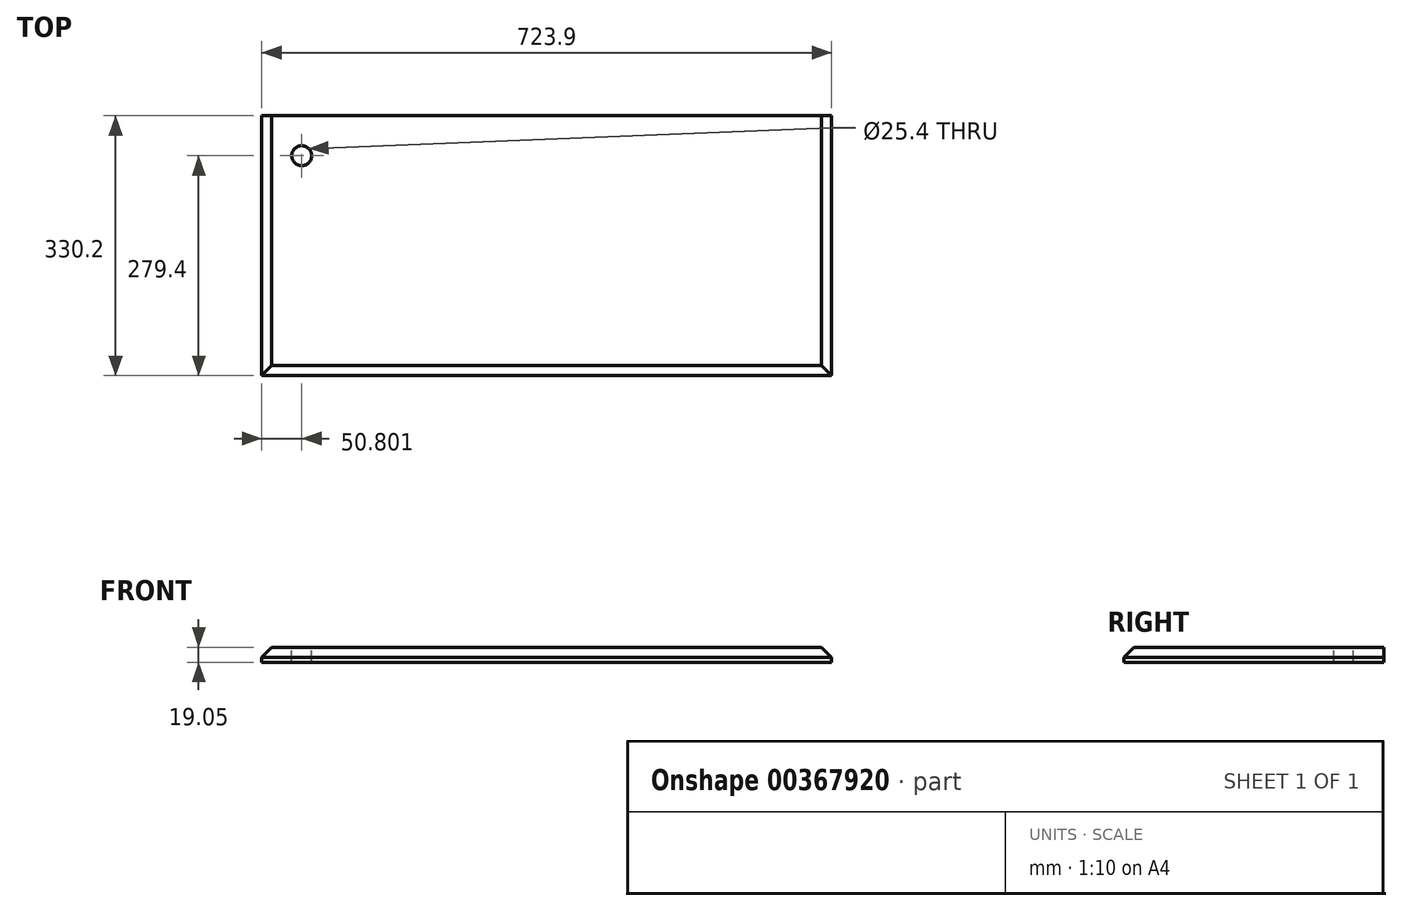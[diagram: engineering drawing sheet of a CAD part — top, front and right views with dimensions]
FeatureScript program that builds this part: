
annotation { "Feature Type Name" : "Feature", "Feature Type Description" : "" }
export const myFeature = defineFeature(function(context is Context, id is Id, definition is map)
    precondition{}
    {
        {
            var Q0;
            Q0=qCreatedBy(makeId("Top.planeOp"),FACE);
            var sketch = newSketch(context, id + "F0", { "sketchPlane" : qUnion([Q0])});
            skLineSegment(sketch, "E0.bottom", {"start": v(-327.98, 161.44) * mm, "end": v(395.92, 161.44) * mm});
            skLineSegment(sketch, "E0.top", {"start": v(-327.98, -168.76) * mm, "end": v(395.92, -168.76) * mm});
            skLineSegment(sketch, "E0.left", {"start": v(-327.98, 161.44) * mm, "end": v(-327.98, -168.76) * mm});
            skLineSegment(sketch, "E0.right", {"start": v(395.92, 161.44) * mm, "end": v(395.92, -168.76) * mm});
            skPoint(sketch, "E1", {"position": v(-277.18, 110.64) * mm});
            skSolve(sketch);
        }
        {
            var Q0;
            Q0 = qSketchRegion(id + "F0", true);
            extrude(context, id + "F1", {"entities" : qUnion([Q0]), "depth" : 19.05 * mm});
        }
        {
            var Q0;
            Q0=makeQuery(id+"F1.opExtrude","CAP_EDGE",EDGE,{"disambiguationData":[OSD([sQuery(id+"F0.wireOp",EDGE,"E0.right")])],"isStart":false});
            var Q1;
            Q1=makeQuery(id+"F1.opExtrude","CAP_EDGE",EDGE,{"disambiguationData":[OSD([sQuery(id+"F0.wireOp",EDGE,"E0.left")])],"isStart":false});
            var Q2;
            Q2=makeQuery(id+"F1.opExtrude","CAP_EDGE",EDGE,{"disambiguationData":[OSD([sQuery(id+"F0.wireOp",EDGE,"E0.top")])],"isStart":false});
            chamfer(context, id + "F2", {"entities" : qUnion([Q0, Q1, Q2]), "width" : 12.7 * mm, "tangentPropagation" : true});
        }
        {
            var Q0;
            Q0=sQuery(id+"F0.wireOp",VERTEX,"E1");
            var Q1;
            Q1=makeQuery(id+"F1.opExtrude","SWEPT_BODY",BODY,{"disambiguationData":[OSD([sQuery(id+"F0.wireOp",EDGE,"E0.bottom"),sQuery(id+"F0.wireOp",EDGE,"E0.top"),sQuery(id+"F0.wireOp",EDGE,"E0.left"),sQuery(id+"F0.wireOp",EDGE,"E0.right")])]});
            hole(context, id + "F3", {"style" : HoleStyle.SIMPLE, "endStyle" : HoleEndStyle.THROUGH, "oppositeDirection" : true, "holeDiameter" : 25.4 * mm, "isTappedThrough" : true, "tappedDepth" : 12.7 * mm, "tapClearance" : 3, "locations" : qUnion([Q0]), "scope" : qUnion([Q1])});
        }
    });
